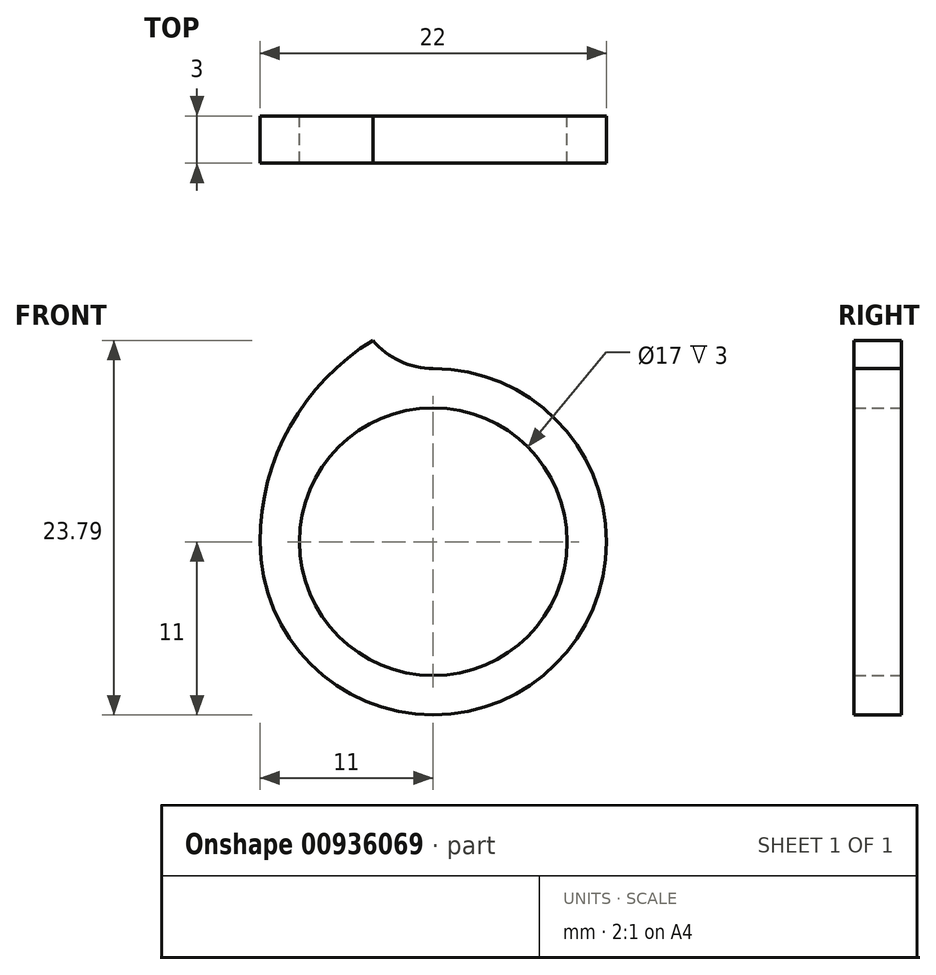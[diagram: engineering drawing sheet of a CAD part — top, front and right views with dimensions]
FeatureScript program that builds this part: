
annotation { "Feature Type Name" : "Feature", "Feature Type Description" : "" }
export const myFeature = defineFeature(function(context is Context, id is Id, definition is map)
    precondition{}
    {
        {
            var Q0;
            Q0=qCreatedBy(makeId("Front.planeOp"),FACE);
            var sketch = newSketch(context, id + "F0", { "sketchPlane" : qUnion([Q0])});
            skCircle(sketch, "E0", {"center": v(0, 0) * mm, "radius": 8.5 * mm});
            skArc(sketch, "E1", {"start": v(-11, 0) * mm, "mid": v(7.78, -7.78) * mm, "end": v(0, 11) * mm});
            skArc(sketch, "E2", {"start": v(-3.83, 12.8) * mm, "mid": v(-2.12, 11.47) * mm, "end": v(0, 11) * mm});
            skArc(sketch, "E3", {"start": v(-3.83, 12.8) * mm, "mid": v(-9.09, 7.33) * mm, "end": v(-11, 0) * mm});
            skSolve(sketch);
        }
        {
            var Q0;
            Q0=makeQuery(id+"F0.imprint","IMPRINT",FACE,{"disambiguationData":[TD([[makeQuery(id+"F0.imprint","IMPRINT",EDGE,{"derivedFrom":sQuery(id+"F0.wireOp",EDGE,"E0")}),-1.0]])]});
            extrude(context, id + "F1", {"entities" : qUnion([Q0]), "depth" : 3 * mm, "offsetDistance" : 25 * mm});
        }
    });
